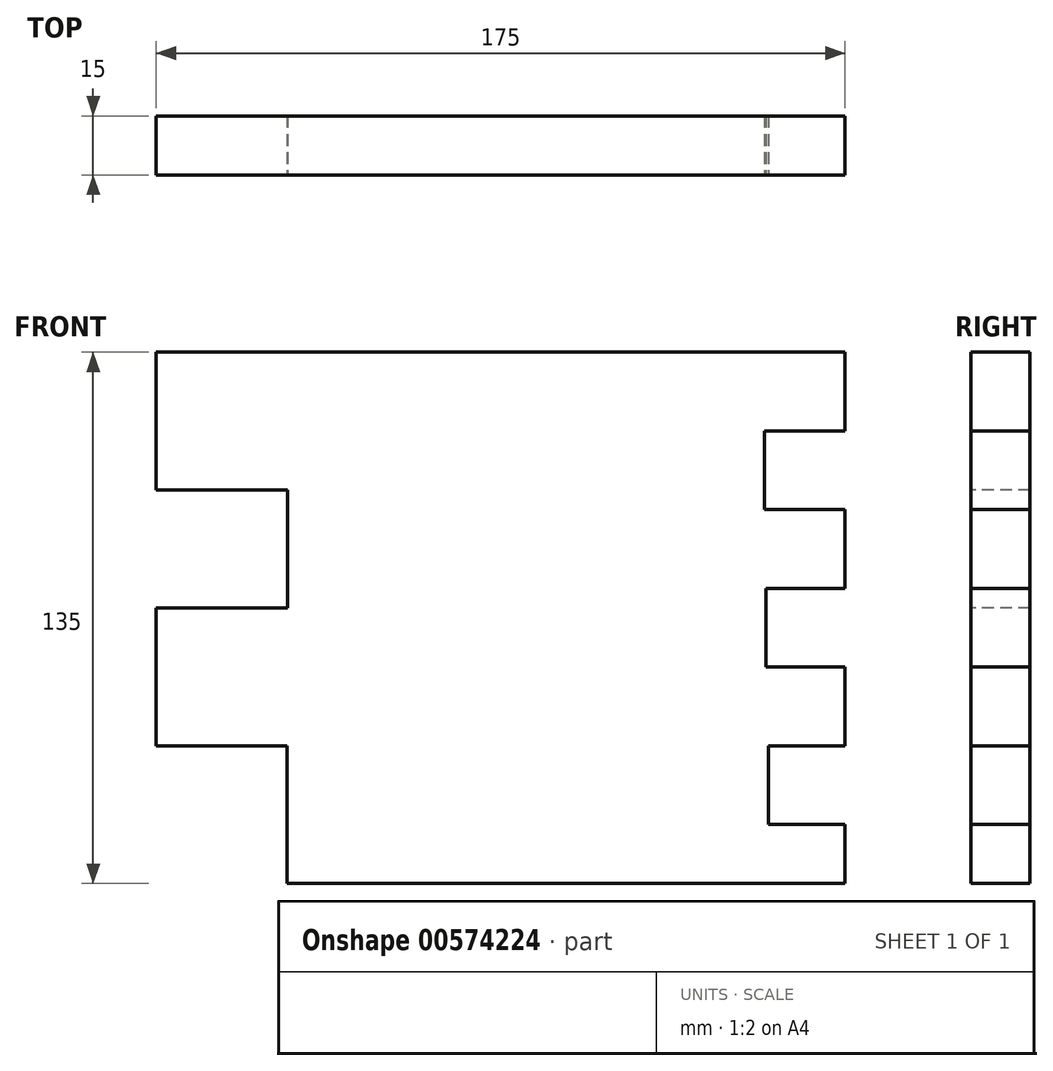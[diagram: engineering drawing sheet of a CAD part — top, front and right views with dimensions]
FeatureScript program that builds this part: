
annotation { "Feature Type Name" : "Feature", "Feature Type Description" : "" }
export const myFeature = defineFeature(function(context is Context, id is Id, definition is map)
    precondition{}
    {
        {
            var Q0;
            Q0=qCreatedBy(makeId("Front.planeOp"),FACE);
            var sketch = newSketch(context, id + "F0", { "sketchPlane" : qUnion([Q0])});
            skLineSegment(sketch, "E0.bottom", {"start": v(-84.6, -58.43) * mm, "end": v(90.4, -58.43) * mm});
            skLineSegment(sketch, "E0.top", {"start": v(-84.6, 76.57) * mm, "end": v(90.4, 76.57) * mm});
            skLineSegment(sketch, "E0.left", {"start": v(-84.6, -58.43) * mm, "end": v(-84.6, 76.57) * mm});
            skLineSegment(sketch, "E0.right", {"start": v(90.4, -58.43) * mm, "end": v(90.4, 76.57) * mm});
            skSolve(sketch);
        }
        {
            var Q0;
            Q0 = qSketchRegion(id + "F0", true);
            extrude(context, id + "F1", {"entities" : qUnion([Q0]), "oppositeDirection" : true, "depth" : 15 * mm, "offsetDistance" : 25.4 * mm});
        }
        {
            var Q0;
            Q0=makeQuery(id+"F1.opExtrude","CAP_FACE",FACE,{"disambiguationData":[OSD([sQuery(id+"F0.wireOp",EDGE,"E0.bottom"),sQuery(id+"F0.wireOp",EDGE,"E0.top"),sQuery(id+"F0.wireOp",EDGE,"E0.left"),sQuery(id+"F0.wireOp",EDGE,"E0.right")])],"isStart":true});
            var sketch = newSketch(context, id + "F2", { "sketchPlane" : qUnion([Q0])});
            skLineSegment(sketch, "E1", {"start": v(-84.6, 76.57) * mm, "end": v(-84.6, 41.57) * mm});
            skLineSegment(sketch, "E2", {"start": v(-84.6, 41.57) * mm, "end": v(-51.19, 41.57) * mm});
            skLineSegment(sketch, "E3", {"start": v(-51.19, 41.57) * mm, "end": v(-51.19, 11.57) * mm});
            skLineSegment(sketch, "E4", {"start": v(-51.19, 11.57) * mm, "end": v(-84.6, 11.57) * mm});
            skLineSegment(sketch, "E5", {"start": v(-84.6, 11.57) * mm, "end": v(-84.6, -23.43) * mm});
            skLineSegment(sketch, "E6", {"start": v(-84.6, -23.43) * mm, "end": v(-51.42, -23.43) * mm});
            skLineSegment(sketch, "E7", {"start": v(-51.42, -23.43) * mm, "end": v(-51.42, -58.43) * mm});
            skSolve(sketch);
        }
        {
            var Q0;
            Q0 = qSketchRegion(id + "F2", true);
            var Q1;
            {var subQ0=sQuery(id+"F2.wireOp",EDGE,"E6");Q1=makeQuery(id+"F2.imprint","IMPRINT",FACE,{"disambiguationData":[TD([[makeQuery(id+"F2.imprint","IMPRINT",EDGE,{"derivedFrom":subQ0}),-1.0]])]});}
            var Q2;
            {var subQ0=sQuery(id+"F2.wireOp",EDGE,"E2");Q2=makeQuery(id+"F2.imprint","IMPRINT",FACE,{"disambiguationData":[TD([[makeQuery(id+"F2.imprint","IMPRINT",EDGE,{"derivedFrom":subQ0}),-1.0]])]});}
            extrude(context, id + "F3", {"entities" : qUnion([Q0, Q1, Q2]), "operationType" : NewBodyOperationType.REMOVE, "endBound" : BoundingType.THROUGH_ALL, "oppositeDirection" : true, "depth" : 25.4 * mm, "offsetDistance" : 25.4 * mm});
        }
        {
            var Q0;
            Q0=makeQuery(id+"F1.opExtrude","CAP_FACE",FACE,{"disambiguationData":[OSD([sQuery(id+"F0.wireOp",EDGE,"E0.bottom"),sQuery(id+"F0.wireOp",EDGE,"E0.top"),sQuery(id+"F0.wireOp",EDGE,"E0.left"),sQuery(id+"F0.wireOp",EDGE,"E0.right")])],"isStart":true});
            var sketch = newSketch(context, id + "F4", { "sketchPlane" : qUnion([Q0])});
            skLineSegment(sketch, "E8", {"start": v(90.4, 76.57) * mm, "end": v(90.4, 56.57) * mm});
            skLineSegment(sketch, "E9", {"start": v(90.4, 56.57) * mm, "end": v(69.97, 56.57) * mm});
            skLineSegment(sketch, "E10", {"start": v(69.97, 56.57) * mm, "end": v(69.97, 36.57) * mm});
            skLineSegment(sketch, "E11", {"start": v(69.97, 36.57) * mm, "end": v(90.4, 36.57) * mm});
            skLineSegment(sketch, "E12", {"start": v(90.4, 36.57) * mm, "end": v(90.4, 16.57) * mm});
            skLineSegment(sketch, "E13", {"start": v(90.4, 16.57) * mm, "end": v(70.3, 16.57) * mm});
            skLineSegment(sketch, "E14", {"start": v(70.3, 16.57) * mm, "end": v(70.3, -3.43) * mm});
            skLineSegment(sketch, "E15", {"start": v(70.3, -3.43) * mm, "end": v(90.4, -3.43) * mm});
            skLineSegment(sketch, "E16", {"start": v(90.4, -3.43) * mm, "end": v(90.4, -23.43) * mm});
            skLineSegment(sketch, "E17", {"start": v(90.4, -23.43) * mm, "end": v(70.96, -23.43) * mm});
            skLineSegment(sketch, "E18", {"start": v(70.96, -23.43) * mm, "end": v(70.96, -43.43) * mm});
            skLineSegment(sketch, "E19", {"start": v(70.96, -43.43) * mm, "end": v(90.4, -43.43) * mm});
            skSolve(sketch);
        }
        {
            var Q0;
            {var subQ0=sQuery(id+"F4.wireOp",EDGE,"E9");Q0=makeQuery(id+"F4.imprint","IMPRINT",FACE,{"disambiguationData":[TD([[makeQuery(id+"F4.imprint","IMPRINT",EDGE,{"derivedFrom":subQ0}),1.0]])]});}
            var Q1;
            {var subQ0=sQuery(id+"F4.wireOp",EDGE,"E13");Q1=makeQuery(id+"F4.imprint","IMPRINT",FACE,{"disambiguationData":[TD([[makeQuery(id+"F4.imprint","IMPRINT",EDGE,{"derivedFrom":subQ0}),1.0]])]});}
            var Q2;
            {var subQ0=sQuery(id+"F4.wireOp",EDGE,"E17");Q2=makeQuery(id+"F4.imprint","IMPRINT",FACE,{"disambiguationData":[TD([[makeQuery(id+"F4.imprint","IMPRINT",EDGE,{"derivedFrom":subQ0}),1.0]])]});}
            extrude(context, id + "F5", {"entities" : qUnion([Q0, Q1, Q2]), "operationType" : NewBodyOperationType.REMOVE, "endBound" : BoundingType.THROUGH_ALL, "oppositeDirection" : true, "depth" : 25.4 * mm, "offsetDistance" : 25.4 * mm});
        }
    });
